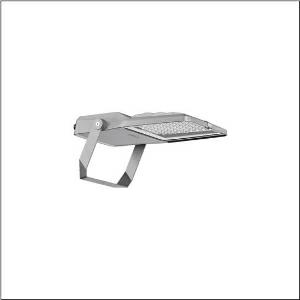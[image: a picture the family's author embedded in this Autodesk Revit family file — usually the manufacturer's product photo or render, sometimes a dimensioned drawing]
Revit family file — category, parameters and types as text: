
# Revit family: floodlight_fl_21_iq_mini___rs12_5xa7772b2b1a_75ed
name_source: partatom
category: Lighting Fixtures
units: mm (PartAtom-declared; Revit-internal decimal feet)

## family parameters
Cut with Voids When Loaded = No
Host = Face
Light Source = No
Part Type = Normal
Room Calculation Point = No
Round Connector Dimension = Use Diameter
Shared = No

## types (1)
- --- (1 x LED, 6300 lm, 45.5 W, 3000K)
    Apparent Load = 46 VA
    CIE Flux Codes = 79 92 99 100 100
    Color Rendering = 70
    Color Temperature = 3000K
    Default Elevation = 1800 mm
    Description = Floodlight FL 21 iQ mini, floodlight, primary light control with lens, of PMMA, primary optical cover: protective disc, of toughened safety glass, transparent, light distribution: RS12, light emission: direct distribution, installation type: surface-mounted, LED, High Power LED, rated luminous flux: 6.300lm, luminous efficacy: 139lm/W, light colour: 730, colour temperature: 3000K, control gear: iQ Street-Remote/DALI, control: Street-Remote, Auto-Match, Temp-Guard, Night-Set, Smart-Wire, Desk-Remote (wireless, voltage-free reading and setting of iQ features in the workshop via application-optimized NFC function/RFID function), optimised constant luminous flux control (CLO 2.0), with terminal, 6-pole, mains connection: 220..240V, AC, 50/60Hz, start of lifetime: 46W, end of service life: 48W, reduction: 22W, luminaire housing, of diecast aluminium, powder-coated, Siteco® metallic grey (DB 702S), corrosivity category C5 mid according to DIN EN ISO 12944, suitable for swimming pools, chlorine-resistant, sealing non-destructively replaceable, mounting bracket, of steel, galvanised, powder-coated, Siteco® metallic grey (DB 702S), protection rating (complete): IP66, insulation class (complete): insulation class II (safety insulation), certification: CE, ENEC, VDE, protection symbol: D, impact resistance: IK08, permissible operating ambient temperature: -40..+40°C, permissible operating ambient temperature for outdoor applications: -40..+50°C, standard: DIN EN 12944, LABS conformity tested according to VDMA 24364:2018-05, packaging unit: 1 piece

Light Distribution: RS12
    Height = 70 mm
    Lamp = 1 x LED
    Lamp Light Flux = 6300 lm
    Lamp Power = 45.5 W
    Lamp count = 1
    Length = 485 mm
    Luminous efficacy = 138 lm/W
    Manufacturer = Siteco
    ModVariant = No
    Model = 5XA7772B2B1A
    Number of Poles = 1
    OnlyDefault = Yes
    Power Factor = 1
    Product Name = Floodlight FL 21 iQ mini | RS12
    Product group = floodlight | pylon annexe
    ProductGroupID = 6200
    Protection Class = Protection class II
    Protection Degree = IP 66
    RLX_Detail_Level = 1
    RLX_Emergency_Light_Flux = 0 lm
    RLX_Emergency_Type = 0
    RLX_Emergency_Type_DB = No
    RlxData = <blob elided: 90817 chars, md5=02acec23>
    Socket = socket
    Standby Power = 0 W
    System Light Flux = 6300 lm
    System Power = 46 W
    Type Comments = factory setting: luminous flux: 100 % | dim-lin: 254 | 463 mA
    Type Image = l_1006845.jpg
    URL = http://relux.com
    VarID = @adj_167888
    Voltage = 0 V
    Weight = 0.00 kg
    Width = 337 mm

## geometry (parser evidence)
native form markers: Blend x4, Sweep x12
no freeform markers — native parametric forms only
